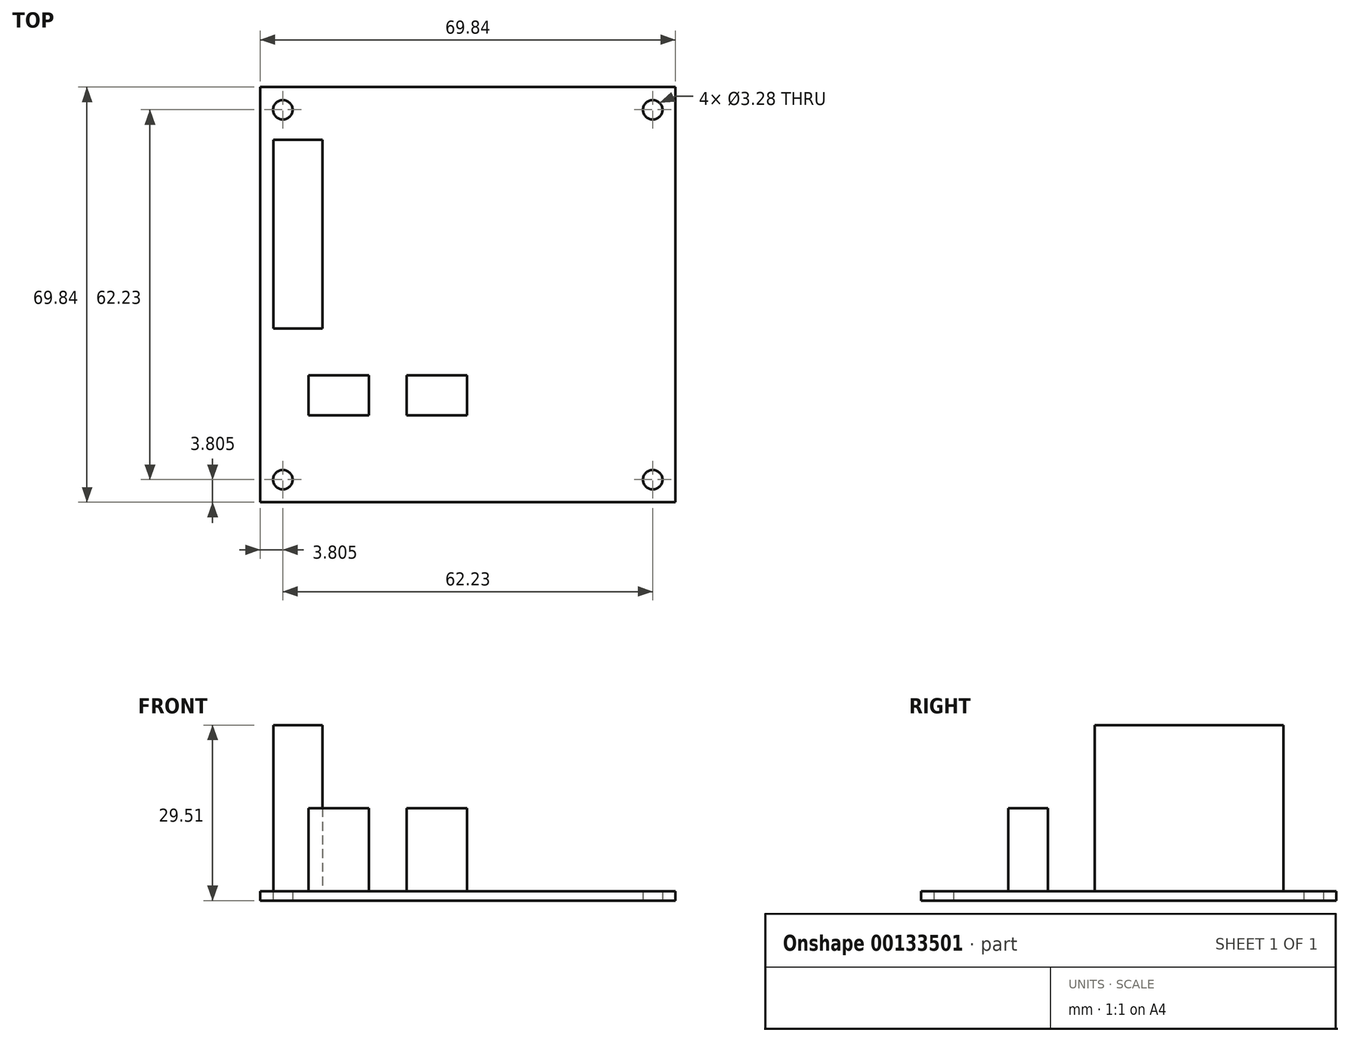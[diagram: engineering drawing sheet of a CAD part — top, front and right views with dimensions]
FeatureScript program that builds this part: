
annotation { "Feature Type Name" : "Feature", "Feature Type Description" : "" }
export const myFeature = defineFeature(function(context is Context, id is Id, definition is map)
    precondition{}
    {
        {
            var Q0;
            Q0=qCreatedBy(makeId("Top.planeOp"),FACE);
            var sketch = newSketch(context, id + "F0", { "sketchPlane" : qUnion([Q0])});
            skLineSegment(sketch, "E0.bottom", {"start": v(34.93, -34.92) * mm, "end": v(-34.93, -34.93) * mm});
            skLineSegment(sketch, "E0.top", {"start": v(34.92, 34.93) * mm, "end": v(-34.93, 34.92) * mm});
            skLineSegment(sketch, "E0.left", {"start": v(34.93, -34.92) * mm, "end": v(34.93, 34.93) * mm});
            skLineSegment(sketch, "E0.right", {"start": v(-34.93, -34.93) * mm, "end": v(-34.93, 34.92) * mm});
            skPoint(sketch, "E0.middle", {"position": v(0, 0) * mm});
            skLineSegment(sketch, "E1.bottom", {"start": v(31.12, -31.11) * mm, "end": v(-31.12, -31.12) * mm, "construction": true});
            skLineSegment(sketch, "E1.top", {"start": v(31.12, 31.12) * mm, "end": v(-31.12, 31.11) * mm, "construction": true});
            skLineSegment(sketch, "E1.left", {"start": v(31.12, -31.12) * mm, "end": v(31.12, 31.12) * mm, "construction": true});
            skLineSegment(sketch, "E1.right", {"start": v(-31.12, -31.12) * mm, "end": v(-31.12, 31.11) * mm, "construction": true});
            skCircle(sketch, "E2", {"center": v(-31.12, 31.11) * mm, "radius": 1.64 * mm});
            skCircle(sketch, "E3", {"center": v(31.12, 31.12) * mm, "radius": 1.64 * mm});
            skCircle(sketch, "E4", {"center": v(31.12, -31.11) * mm, "radius": 1.64 * mm});
            skCircle(sketch, "E5", {"center": v(-31.12, -31.12) * mm, "radius": 1.64 * mm});
            skSolve(sketch);
        }
        {
            var Q0;
            Q0 = qSketchRegion(id + "F0", true);
            extrude(context, id + "F1", {"entities" : qUnion([Q0]), "depth" : 1.57 * mm});
        }
        {
            var Q0;
            Q0=makeQuery(id+"F1.opExtrude","CAP_FACE",FACE,{"disambiguationData":[OSD([sQuery(id+"F0.wireOp",EDGE,"E0.bottom"),sQuery(id+"F0.wireOp",EDGE,"E0.top"),sQuery(id+"F0.wireOp",EDGE,"E0.left"),sQuery(id+"F0.wireOp",EDGE,"E0.right"),sQuery(id+"F0.wireOp",EDGE,"E2"),sQuery(id+"F0.wireOp",EDGE,"E3"),sQuery(id+"F0.wireOp",EDGE,"E4"),sQuery(id+"F0.wireOp",EDGE,"E5")])],"isStart":false});
            var sketch = newSketch(context, id + "F2", { "sketchPlane" : qUnion([Q0])});
            skLineSegment(sketch, "E6.bottom", {"start": v(-32.69, 26.04) * mm, "end": v(-24.46, 26.04) * mm});
            skLineSegment(sketch, "E6.top", {"start": v(-32.69, -5.71) * mm, "end": v(-24.46, -5.71) * mm});
            skLineSegment(sketch, "E6.left", {"start": v(-32.69, 26.04) * mm, "end": v(-32.69, -5.71) * mm});
            skLineSegment(sketch, "E6.right", {"start": v(-24.46, 26.04) * mm, "end": v(-24.46, -5.71) * mm});
            skSolve(sketch);
        }
        {
            var Q0;
            Q0 = qSketchRegion(id + "F2", true);
            extrude(context, id + "F3", {"entities" : qUnion([Q0]), "operationType" : NewBodyOperationType.ADD, "depth" : 27.94 * mm});
        }
        {
            var Q0;
            Q0=makeQuery(id+"F1.opExtrude","CAP_FACE",FACE,{"disambiguationData":[OSD([sQuery(id+"F0.wireOp",EDGE,"E0.bottom"),sQuery(id+"F0.wireOp",EDGE,"E0.top"),sQuery(id+"F0.wireOp",EDGE,"E0.left"),sQuery(id+"F0.wireOp",EDGE,"E0.right"),sQuery(id+"F0.wireOp",EDGE,"E2"),sQuery(id+"F0.wireOp",EDGE,"E3"),sQuery(id+"F0.wireOp",EDGE,"E4"),sQuery(id+"F0.wireOp",EDGE,"E5")])],"isStart":false});
            var sketch = newSketch(context, id + "F4", { "sketchPlane" : qUnion([Q0])});
            skLineSegment(sketch, "E7.bottom", {"start": v(-16.64, -20.3) * mm, "end": v(-26.8, -20.3) * mm});
            skLineSegment(sketch, "E7.top", {"start": v(-16.64, -13.59) * mm, "end": v(-26.8, -13.59) * mm});
            skLineSegment(sketch, "E7.left", {"start": v(-16.64, -20.3) * mm, "end": v(-16.64, -13.59) * mm});
            skLineSegment(sketch, "E7.right", {"start": v(-26.8, -20.3) * mm, "end": v(-26.8, -13.59) * mm});
            skPoint(sketch, "E7.middle", {"position": v(-21.72, -16.94) * mm});
            skLineSegment(sketch, "E8.bottom", {"start": v(-0.13, -20.3) * mm, "end": v(-10.29, -20.3) * mm});
            skLineSegment(sketch, "E8.top", {"start": v(-0.13, -13.59) * mm, "end": v(-10.29, -13.59) * mm});
            skLineSegment(sketch, "E8.left", {"start": v(-0.13, -20.3) * mm, "end": v(-0.13, -13.59) * mm});
            skLineSegment(sketch, "E8.right", {"start": v(-10.29, -20.3) * mm, "end": v(-10.29, -13.59) * mm});
            skPoint(sketch, "E8.middle", {"position": v(-5.2, -16.94) * mm});
            skSolve(sketch);
        }
        {
            var Q0;
            Q0 = qSketchRegion(id + "F4", true);
            extrude(context, id + "F5", {"entities" : qUnion([Q0]), "operationType" : NewBodyOperationType.ADD, "depth" : 13.97 * mm});
        }
    });
